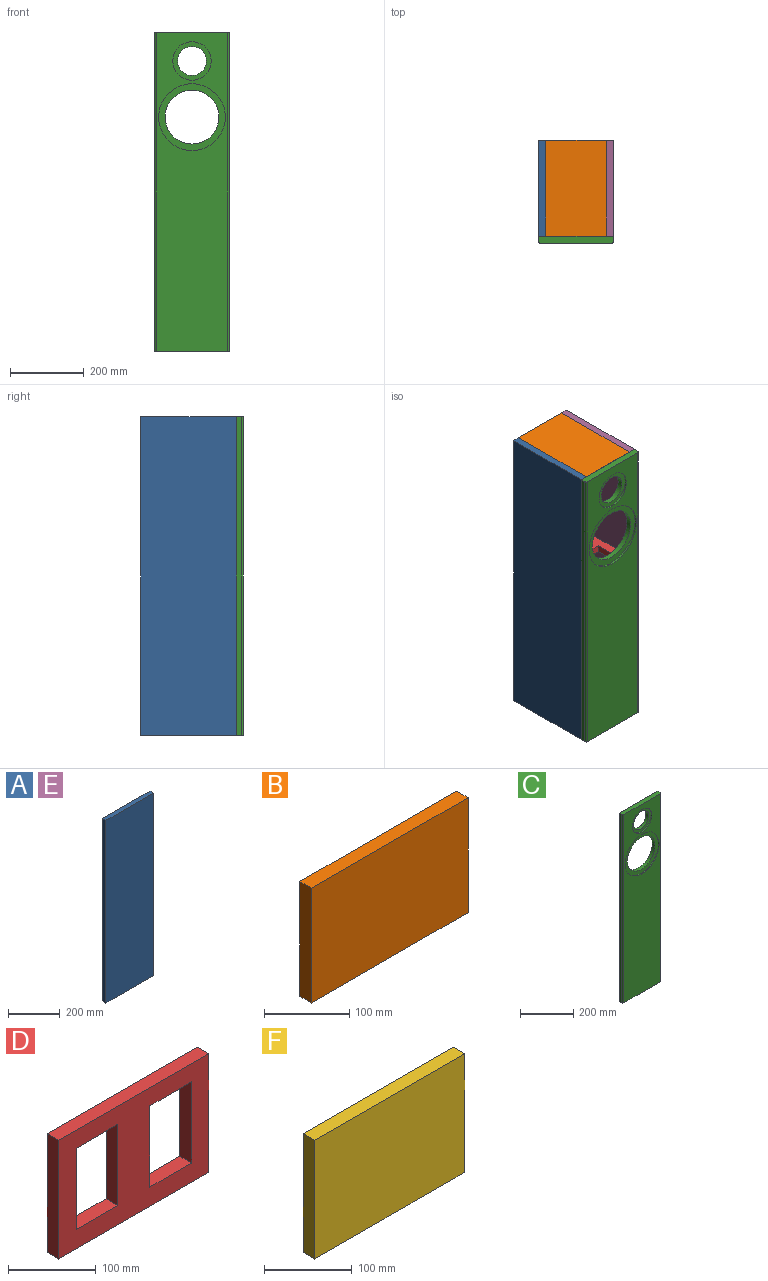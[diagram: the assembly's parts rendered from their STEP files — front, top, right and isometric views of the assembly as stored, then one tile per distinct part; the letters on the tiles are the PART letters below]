
ASSEMBLY  parts=6 mates=8
PART A: 6 faces, bbox 260.4x19.1x863.6 mm
  f0: plane 863.6x19.05mm, normal (-1,0,0), area 16451.6mm2, adj f1,f3,f4,f5
  f1: plane 260.35x19.05mm, normal (0,0,-1), area 4959.7mm2, adj f0,f2,f4,f5
  f2: plane 863.6x19.05mm, normal (1,0,0), area 16451.6mm2, adj f1,f3,f4,f5
  f3: plane 260.35x19.05mm, normal (0,0,1), area 4959.7mm2, adj f0,f2,f4,f5
  f4: plane 863.6x260.35mm, normal (0,1,0), area 224838.3mm2, adj f0,f1,f2,f3
  f5: plane 863.6x260.35mm, normal (0,-1,0), area 224838.3mm2, adj f0,f1,f2,f3
PART B: 6 faces, bbox 260.4x19.1x165.1 mm
  f0: plane 165.1x19.05mm, normal (-1,0,0), area 3145.2mm2, adj f1,f3,f4,f5
  f1: plane 260.35x19.05mm, normal (0,0,-1), area 4959.7mm2, adj f0,f2,f4,f5
  f2: plane 165.1x19.05mm, normal (1,0,0), area 3145.2mm2, adj f1,f3,f4,f5
  f3: plane 260.35x19.05mm, normal (0,0,1), area 4959.7mm2, adj f0,f2,f4,f5
  f4: plane 260.35x165.1mm, normal (0,1,0), area 42983.8mm2, adj f0,f1,f2,f3
  f5: plane 260.35x165.1mm, normal (0,-1,0), area 42983.8mm2, adj f0,f1,f2,f3
PART C: 14 faces, bbox 203.2x19.1x863.6 mm
  f0: plane 863.6x13.97mm, normal (-1,0,0), area 12064.5mm2, adj f1,f3,f4,f13
  f1: plane 203.2x19.05mm, normal (0,0,-1), area 3859.9mm2, adj f0,f2,f4,f5,f12,f13
  f2: plane 863.6x13.97mm, normal (1,0,0), area 12064.5mm2, adj f1,f3,f4,f12
  f3: plane 203.2x19.05mm, normal (0,0,1), area 3859.9mm2, adj f0,f2,f4,f5,f12,f13
  f4: plane 863.6x203.2mm, normal (0,1,0), area 153861mm2, adj f0,f1,f2,f3,f8,f11
  f5: plane 863.6x193.04mm, normal (0,-1,0), area 132435mm2, adj f1,f3,f6,f9,f12,f13
  f6: cylinder r=90.49mm len=180.98mm, axis (0,-1,0), area 2888.2mm2, adj f5,f7
  f7: plane 180.98x180.98mm, normal (0,-1,0), area 8970.3mm2, adj f6,f8
  f8: cylinder r=73.03mm len=146.05mm, axis (0,-1,0), area 6409.8mm2, adj f4,f7
  f9: cylinder r=52.17mm len=104.34mm, axis (0,-1,0), area 1582mm2, adj f5,f10
  f10: plane 104.34x104.34mm, normal (0,-1,0), area 3681.6mm2, adj f9,f11
  f11: cylinder r=39.37mm len=78.74mm, axis (0,-1,0), area 3518.6mm2, adj f4,f10
  f12: cylinder r=5.08mm len=863.6mm, axis (0,0,1), area 6891.2mm2, adj f1,f2,f3,f5
  f13: cylinder r=5.08mm len=863.6mm, axis (0,0,-1), area 6891.2mm2, adj f0,f1,f3,f5
PART D: 14 faces, bbox 241.3x19.1x165.1 mm
  f0: plane 241.3x165.1mm, normal (0,1,0), area 24671.7mm2, adj f2,f3,f4,f5,f6,f7,f8,f9
  f1: plane 241.3x165.1mm, normal (0,-1,0), area 24671.7mm2, adj f2,f3,f4,f5,f6,f7,f8,f9
  f2: plane 165.1x19.05mm, normal (-1,0,0), area 3145.2mm2, adj f0,f1,f3,f5
  f3: plane 241.3x19.05mm, normal (0,0,-1), area 4596.8mm2, adj f0,f1,f2,f4
  f4: plane 165.1x19.05mm, normal (1,0,0), area 3145.2mm2, adj f0,f1,f3,f5
  f5: plane 241.3x19.05mm, normal (0,0,1), area 4596.8mm2, adj f0,f1,f2,f4
  f6: plane 113.1x19.05mm, normal (1,0,0), area 2154.5mm2, adj f0,f1,f7,f9
  f7: plane 67.05x19.05mm, normal (0,0,1), area 1277.4mm2, adj f0,f1,f6,f8
  f8: plane 113.1x19.05mm, normal (-1,0,0), area 2154.5mm2, adj f0,f1,f7,f9
  f9: plane 67.05x19.05mm, normal (0,0,-1), area 1277.4mm2, adj f0,f1,f6,f8
  f10: plane 113.1x19.05mm, normal (1,0,0), area 2154.5mm2, adj f0,f1,f11,f13
  f11: plane 67.05x19.05mm, normal (0,0,1), area 1277.4mm2, adj f0,f1,f10,f12
  f12: plane 113.1x19.05mm, normal (-1,0,0), area 2154.5mm2, adj f0,f1,f11,f13
  f13: plane 67.05x19.05mm, normal (0,0,-1), area 1277.4mm2, adj f0,f1,f10,f12
PART E: same geometry as A
PART F: 6 faces, bbox 241.3x19.1x165.1 mm
  f0: plane 165.1x19.05mm, normal (-1,0,0), area 3145.2mm2, adj f1,f3,f4,f5
  f1: plane 241.3x19.05mm, normal (0,0,-1), area 4596.8mm2, adj f0,f2,f4,f5
  f2: plane 165.1x19.05mm, normal (1,0,0), area 3145.2mm2, adj f1,f3,f4,f5
  f3: plane 241.3x19.05mm, normal (0,0,1), area 4596.8mm2, adj f0,f2,f4,f5
  f4: plane 241.3x165.1mm, normal (0,1,0), area 39838.6mm2, adj f0,f1,f2,f3
  f5: plane 241.3x165.1mm, normal (0,-1,0), area 39838.6mm2, adj f0,f1,f2,f3
PLACE A rot(axis=(0,0,1),90deg) t=(-382.67,189.72,-172.24)mm
PLACE B rot(axis=(0.58,0.58,0.58),120deg) t=(-382.67,189.72,672.31)mm
PLACE C rot(axis=(0.32,-0.41,-0.85),0deg) t=(-401.72,170.67,-172.24)mm
PLACE D rot(axis=(-0.58,0.58,-0.58),120deg) t=(-382.67,431.02,344.92)mm
PLACE E rot(axis=(0,0,1),90deg) t=(-198.52,189.72,-172.24)mm
PLACE F rot(axis=(-0.58,0.58,-0.58),120deg) t=(-382.67,431.02,-153.19)mm
MATE parallel E.f0 <-> C.f4  axis (0,-1,0) through (-208.04,189.72,259.56)mm
MATE parallel B.f4 <-> E.f3  axis (0,0,1) through (-217.57,189.72,691.36)mm
MATE planar D.f4 <-> C.f4  axis (0,-1,0) through (-300.12,189.72,335.4)mm
MATE planar C.f3 <-> E.f3  axis (0,0,1) through (-300.12,180.22,691.36)mm
MATE planar C.f2 <-> E.f5  axis (1,0,0) through (-198.52,182.73,259.56)mm
MATE parallel C.f4 <-> E.f0  axis (0,1,0) through (-300.12,189.72,226.18)mm
MATE parallel F.f4 <-> E.f1  axis (0,0,-1) through (-217.57,189.72,-172.24)mm
MATE parallel A.f3 <-> C.f3  axis (0,0,1) through (-401.72,189.72,691.36)mm
